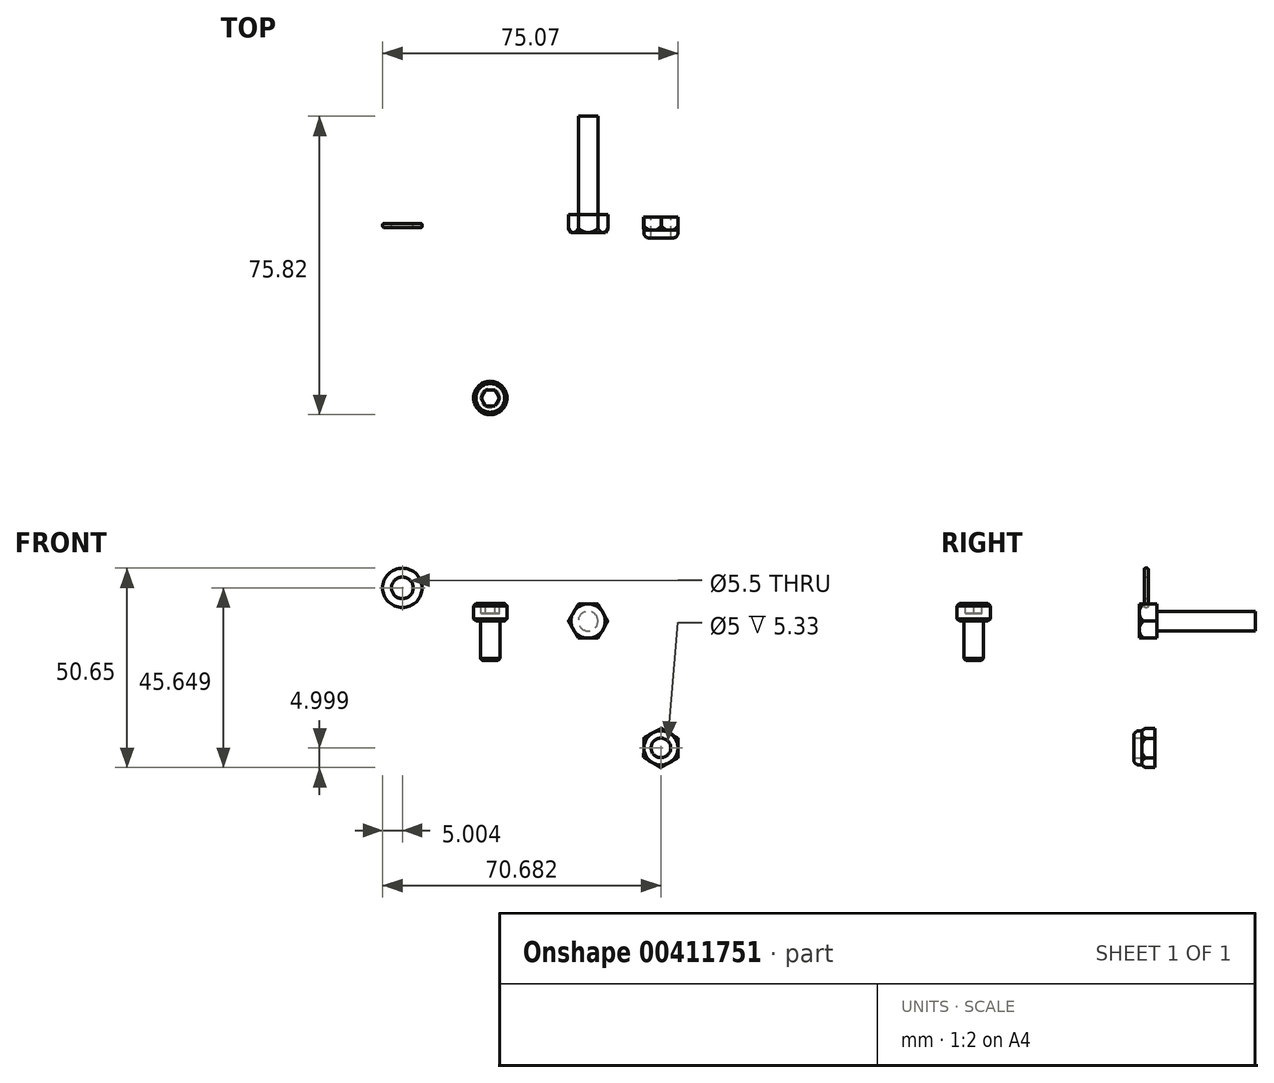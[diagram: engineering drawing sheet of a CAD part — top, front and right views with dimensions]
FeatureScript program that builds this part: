
annotation { "Feature Type Name" : "Feature", "Feature Type Description" : "" }
export const myFeature = defineFeature(function(context is Context, id is Id, definition is map)
    precondition{}
    {
        {
            var Q0;
            Q0=qCreatedBy(makeId("Front.planeOp"),FACE);
            var sketch = newSketch(context, id + "F0", { "sketchPlane" : qUnion([Q0])});
            skCircle(sketch, "E0.cCircle", {"center": v(0, 0) * mm, "radius": 4.33 * mm, "construction": true});
            skLineSegment(sketch, "E0.0", {"start": v(-2.5, 4.33) * mm, "end": v(2.5, 4.33) * mm});
            skLineSegment(sketch, "E0.1", {"start": v(2.5, 4.33) * mm, "end": v(5, 0) * mm});
            skLineSegment(sketch, "E0.2", {"start": v(5, 0) * mm, "end": v(2.5, -4.33) * mm});
            skLineSegment(sketch, "E0.3", {"start": v(2.5, -4.33) * mm, "end": v(-2.5, -4.33) * mm});
            skLineSegment(sketch, "E0.4", {"start": v(-2.5, -4.33) * mm, "end": v(-5, 0) * mm});
            skLineSegment(sketch, "E0.5", {"start": v(-5, 0) * mm, "end": v(-2.5, 4.33) * mm});
            skPoint(sketch, "E0.0.midPoint", {"position": v(0, 4.33) * mm});
            skSolve(sketch);
        }
        {
            var Q0;
            Q0=makeQuery(id+"F0.imprint","IMPRINT",FACE,{"disambiguationData":[TD([[makeQuery(id+"F0.imprint","IMPRINT",EDGE,{"derivedFrom":sQuery(id+"F0.wireOp",EDGE,"E0.0")}),-1.0]])]});
            extrude(context, id + "F1", {"entities" : qUnion([Q0]), "endBound" : BoundingType.SYMMETRIC, "depth" : 4.5 * mm});
        }
        {
            var Q0;
            Q0=makeQuery(id+"F1.opExtrude","SWEPT_FACE",FACE,{"disambiguationData":[OSD([sQuery(id+"F0.wireOp",EDGE,"E0.4")])]});
            var sketch = newSketch(context, id + "F2", { "sketchPlane" : qUnion([Q0])});
            skLineSegment(sketch, "E1", {"start": v(2.25, -2.5) * mm, "end": v(1.4, -2.5) * mm});
            skLineSegment(sketch, "E2", {"start": v(1.4, -2.5) * mm, "end": v(2.25, -1.9) * mm});
            skLineSegment(sketch, "E3", {"start": v(2.25, -1.9) * mm, "end": v(2.25, -2.5) * mm});
            skSolve(sketch);
        }
        {
            var Q0;
            Q0=qCreatedBy(makeId("Top.planeOp"),FACE);
            var sketch = newSketch(context, id + "F3", { "sketchPlane" : qUnion([Q0])});
            skLineSegment(sketch, "E4", {"start": v(5, -1.23) * mm, "end": v(5, -2.4) * mm});
            skLineSegment(sketch, "E5", {"start": v(5, -2.4) * mm, "end": v(4.27, -2.4) * mm});
            skLineSegment(sketch, "E6", {"start": v(4.27, -2.4) * mm, "end": v(5, -1.23) * mm});
            skSolve(sketch);
        }
        {
            var Q0;
            Q0=makeQuery(id+"F3.imprint","IMPRINT",FACE,{"disambiguationData":[TD([[makeQuery(id+"F3.imprint","IMPRINT",EDGE,{"derivedFrom":sQuery(id+"F3.wireOp",EDGE,"E4")}),-1.0]])]});
            var Q1;
            Q1=sQuery(id+"F0.wireOp",EDGE,"E0.cCircle");
            revolve(context, id + "F4", {"operationType" : NewBodyOperationType.REMOVE, "entities" : qUnion([Q0]), "axis" : qUnion([Q1]), "revolveType" : RevolveType.FULL, "oppositeDirection" : true});
        }
        {
            var Q0;
            Q0=makeQuery(id+"F1.opExtrude","CAP_FACE",FACE,{"disambiguationData":[OSD([sQuery(id+"F0.wireOp",EDGE,"E0.0"),sQuery(id+"F0.wireOp",EDGE,"E0.1"),sQuery(id+"F0.wireOp",EDGE,"E0.2"),sQuery(id+"F0.wireOp",EDGE,"E0.3"),sQuery(id+"F0.wireOp",EDGE,"E0.4"),sQuery(id+"F0.wireOp",EDGE,"E0.5")])],"isStart":true});
            var sketch = newSketch(context, id + "F5", { "sketchPlane" : qUnion([Q0])});
            skCircle(sketch, "E7", {"center": v(0, 0) * mm, "radius": 2.5 * mm});
            skSolve(sketch);
        }
        {
            var Q0;
            Q0=makeQuery(id+"F5.imprint","IMPRINT",FACE,{"disambiguationData":[TD([[makeQuery(id+"F5.imprint","IMPRINT",EDGE,{"derivedFrom":sQuery(id+"F5.wireOp",EDGE,"E7")}),1.0]])]});
            extrude(context, id + "F6", {"entities" : qUnion([Q0]), "operationType" : NewBodyOperationType.ADD, "depth" : 25 * mm});
        }
        {
            var Q0;
            Q0=qCreatedBy(makeId("Front.planeOp"),FACE);
            var sketch = newSketch(context, id + "F7", { "sketchPlane" : qUnion([Q0])});
            skCircle(sketch, "E8", {"center": v(-47.19, 8.45) * mm, "radius": 5 * mm});
            skCircle(sketch, "E9", {"center": v(-47.19, 8.45) * mm, "radius": 2.75 * mm});
            skSolve(sketch);
        }
        {
            var Q0;
            Q0=makeQuery(id+"F7.imprint","IMPRINT",FACE,{"disambiguationData":[TD([[makeQuery(id+"F7.imprint","IMPRINT",EDGE,{"derivedFrom":sQuery(id+"F7.wireOp",EDGE,"E8")}),1.0]])]});
            extrude(context, id + "F8", {"entities" : qUnion([Q0]), "depth" : 1 * mm});
        }
        {
            var Q0;
            Q0=makeQuery(id+"F8.opExtrude","CAP_EDGE",EDGE,{"disambiguationData":[OSD([sQuery(id+"F7.wireOp",EDGE,"E8")])],"isStart":false});
            var Q1;
            Q1=makeQuery(id+"F8.opExtrude","CAP_EDGE",EDGE,{"disambiguationData":[OSD([sQuery(id+"F7.wireOp",EDGE,"E8")])],"isStart":true});
            fillet(context, id + "F9", {"entities" : qUnion([Q0, Q1]), "radius" : 0.3 * mm, "tangentPropagation" : true, "allowEdgeOverflow" : false});
        }
        {
            var Q0;
            Q0=qCreatedBy(makeId("Front.planeOp"),FACE);
            var sketch = newSketch(context, id + "F10", { "sketchPlane" : qUnion([Q0])});
            skCircle(sketch, "E10.cCircle", {"center": v(18.5, -32.2) * mm, "radius": 4.33 * mm, "construction": true});
            skLineSegment(sketch, "E10.0", {"start": v(18.6, -27.2) * mm, "end": v(22.88, -29.8) * mm});
            skLineSegment(sketch, "E10.1", {"start": v(22.88, -29.8) * mm, "end": v(22.77, -34.8) * mm});
            skLineSegment(sketch, "E10.2", {"start": v(22.77, -34.8) * mm, "end": v(18.38, -37.2) * mm});
            skLineSegment(sketch, "E10.3", {"start": v(18.38, -37.2) * mm, "end": v(14.1, -34.6) * mm});
            skLineSegment(sketch, "E10.4", {"start": v(14.1, -34.6) * mm, "end": v(14.22, -29.6) * mm});
            skLineSegment(sketch, "E10.5", {"start": v(14.22, -29.6) * mm, "end": v(18.6, -27.2) * mm});
            skPoint(sketch, "E10.0.midPoint", {"position": v(20.74, -28.5) * mm});
            skCircle(sketch, "E11", {"center": v(18.5, -32.2) * mm, "radius": 2.5 * mm});
            skSolve(sketch);
        }
        {
            var Q0;
            Q0=makeQuery(id+"F10.imprint","IMPRINT",FACE,{"disambiguationData":[TD([[makeQuery(id+"F10.imprint","IMPRINT",EDGE,{"derivedFrom":sQuery(id+"F10.wireOp",EDGE,"E10.0")}),-1.0]])]});
            extrude(context, id + "F11", {"entities" : qUnion([Q0]), "endBound" : BoundingType.SYMMETRIC, "depth" : 3.33 * mm});
        }
        {
            var Q0;
            Q0=qCreatedBy(makeId("Right.planeOp"),FACE);
            cPlane(context, id + "F12", {"entities" : qUnion([Q0]), "cplaneType" : CPlaneType.OFFSET, "offset" : 18.4 * mm, "width" : 150 * mm, "height" : 150 * mm});
        }
        {
            var Q0;
            Q0=qCreatedBy(id+"F12.planeOp",FACE);
            var sketch = newSketch(context, id + "F13", { "sketchPlane" : qUnion([Q0])});
            skLineSegment(sketch, "E12", {"start": v(-0.6, -37.21) * mm, "end": v(-1.74, -37.21) * mm});
            skLineSegment(sketch, "E13", {"start": v(-1.74, -37.21) * mm, "end": v(-1.75, -36.57) * mm});
            skLineSegment(sketch, "E14", {"start": v(-1.75, -36.57) * mm, "end": v(-0.6, -37.21) * mm});
            skSolve(sketch);
        }
        {
            var Q0;
            Q0=makeQuery(id+"F13.imprint","IMPRINT",FACE,{"disambiguationData":[TD([[makeQuery(id+"F13.imprint","IMPRINT",EDGE,{"derivedFrom":sQuery(id+"F13.wireOp",EDGE,"E12")}),-1.0]])]});
            var Q1;
            Q1=makeQuery(id+"F11.opExtrude","CAP_EDGE",EDGE,{"disambiguationData":[OSD([sQuery(id+"F10.wireOp",EDGE,"E11")])],"isStart":false});
            revolve(context, id + "F14", {"operationType" : NewBodyOperationType.REMOVE, "entities" : qUnion([Q0]), "axis" : qUnion([Q1]), "revolveType" : RevolveType.FULL, "oppositeDirection" : true});
        }
        {
            var Q0;
            {var subQ0=sQuery(id+"F10.wireOp",EDGE,"E10.2");var subQ1=sQuery(id+"F10.wireOp",EDGE,"E10.1");var subQ2=sQuery(id+"F10.wireOp",EDGE,"E10.3");var subQ3=sQuery(id+"F10.wireOp",EDGE,"E10.0");var subQ4=sQuery(id+"F10.wireOp",EDGE,"E10.4");var subQ5=sQuery(id+"F10.wireOp",EDGE,"E10.5");var subQ6=sQuery(id+"F10.wireOp",EDGE,"E11");Q0=makeQuery(id+"F14.boolean.opBoolean","SPLIT",FACE,{"disambiguationData":[TD([makeQuery(id+"F11.opExtrude","SWEPT_FACE",FACE,{"disambiguationData":[OSD([subQ3])]}),makeQuery(id+"F11.opExtrude","SWEPT_FACE",FACE,{"disambiguationData":[OSD([subQ1])]}),makeQuery(id+"F11.opExtrude","SWEPT_FACE",FACE,{"disambiguationData":[OSD([subQ0])]}),makeQuery(id+"F11.opExtrude","SWEPT_FACE",FACE,{"disambiguationData":[OSD([subQ2])]}),makeQuery(id+"F11.opExtrude","SWEPT_FACE",FACE,{"disambiguationData":[OSD([subQ4])]}),makeQuery(id+"F11.opExtrude","SWEPT_FACE",FACE,{"disambiguationData":[OSD([subQ5])]}),makeQuery(id+"F11.opExtrude","SWEPT_FACE",FACE,{"disambiguationData":[OSD([subQ6])]}),makeQuery(id+"F14.opRevolve","SWEPT_FACE",FACE,{"disambiguationData":[OSD([sQuery(id+"F13.wireOp",EDGE,"E14")])]})])],"derivedFrom":makeQuery(id+"F11.opExtrude","CAP_FACE",FACE,{"disambiguationData":[OSD([subQ3,subQ1,subQ0,subQ2,subQ4,subQ5,subQ6])],"isStart":false})});}
            var sketch = newSketch(context, id + "F15", { "sketchPlane" : qUnion([Q0])});
            skCircle(sketch, "E15.0", {"center": v(18.5, -32.2) * mm, "radius": 4.33 * mm});
            skSolve(sketch);
        }
        {
            var Q0;
            {var subQ1=sQuery(id+"F10.wireOp",EDGE,"E11");Q0=makeQuery(id+"F15.imprint","IMPRINT",FACE,{"disambiguationData":[TD([[makeQuery(id+"F15.imprint","IMPRINT",EDGE,{"derivedFrom":makeQuery(id+"F11.opExtrude","CAP_EDGE",EDGE,{"disambiguationData":[OSD([subQ1])],"isStart":false})}),-1.0]])]});}
            extrude(context, id + "F16", {"entities" : qUnion([Q0]), "operationType" : NewBodyOperationType.ADD, "depth" : 2 * mm});
        }
        {
            var Q0;
            Q0=makeQuery(id+"F16.opExtrude","CAP_EDGE",EDGE,{"disambiguationData":[OSD([sQuery(id+"F15.wireOp",EDGE,"E15.0")])],"isStart":false});
            fillet(context, id + "F17", {"entities" : qUnion([Q0]), "radius" : 1.3 * mm, "tangentPropagation" : true, "allowEdgeOverflow" : false});
        }
        {
            var Q0;
            Q0=qCreatedBy(makeId("Top.planeOp"),FACE);
            var sketch = newSketch(context, id + "F18", { "sketchPlane" : qUnion([Q0])});
            skCircle(sketch, "E16", {"center": v(-24.87, -44.32) * mm, "radius": 4.25 * mm});
            skSolve(sketch);
        }
        {
            var Q0;
            Q0=makeQuery(id+"F18.imprint","IMPRINT",FACE,{"disambiguationData":[TD([[makeQuery(id+"F18.imprint","IMPRINT",EDGE,{"derivedFrom":sQuery(id+"F18.wireOp",EDGE,"E16")}),1.0]])]});
            extrude(context, id + "F19", {"entities" : qUnion([Q0]), "depth" : 4.5 * mm});
        }
        {
            var Q0;
            Q0=makeQuery(id+"F19.opExtrude","CAP_FACE",FACE,{"disambiguationData":[OSD([sQuery(id+"F18.wireOp",EDGE,"E16")])],"isStart":false});
            var sketch = newSketch(context, id + "F20", { "sketchPlane" : qUnion([Q0])});
            skCircle(sketch, "E17.cCircle", {"center": v(-24.87, -44.32) * mm, "radius": 2.07 * mm, "construction": true});
            skLineSegment(sketch, "E17.0", {"start": v(-23.66, -42.25) * mm, "end": v(-22.48, -44.33) * mm});
            skLineSegment(sketch, "E17.1", {"start": v(-22.48, -44.33) * mm, "end": v(-23.68, -46.4) * mm});
            skLineSegment(sketch, "E17.2", {"start": v(-23.68, -46.4) * mm, "end": v(-26.07, -46.38) * mm});
            skLineSegment(sketch, "E17.3", {"start": v(-26.07, -46.38) * mm, "end": v(-27.26, -44.3) * mm});
            skLineSegment(sketch, "E17.4", {"start": v(-27.26, -44.3) * mm, "end": v(-26.06, -42.24) * mm});
            skLineSegment(sketch, "E17.5", {"start": v(-26.06, -42.24) * mm, "end": v(-23.66, -42.25) * mm});
            skPoint(sketch, "E17.0.midPoint", {"position": v(-23.07, -43.29) * mm});
            skSolve(sketch);
        }
        {
            var Q0;
            Q0=makeQuery(id+"F19.opExtrude","CAP_EDGE",EDGE,{"disambiguationData":[OSD([sQuery(id+"F18.wireOp",EDGE,"E16")])],"isStart":false});
            var Q1;
            Q1=makeQuery(id+"F19.opExtrude","CAP_EDGE",EDGE,{"disambiguationData":[OSD([sQuery(id+"F18.wireOp",EDGE,"E16")])],"isStart":true});
            chamfer(context, id + "F21", {"entities" : qUnion([Q0, Q1]), "width" : 0.6 * mm, "tangentPropagation" : true});
        }
        {
            var Q0;
            Q0=makeQuery(id+"F20.imprint","IMPRINT",FACE,{"disambiguationData":[TD([[makeQuery(id+"F20.imprint","IMPRINT",EDGE,{"derivedFrom":sQuery(id+"F20.wireOp",EDGE,"E17.0")}),-1.0]])]});
            extrude(context, id + "F22", {"entities" : qUnion([Q0]), "operationType" : NewBodyOperationType.REMOVE, "oppositeDirection" : true, "depth" : 2.6 * mm});
        }
        {
            var Q0;
            Q0=makeQuery(id+"F19.opExtrude","CAP_FACE",FACE,{"disambiguationData":[OSD([sQuery(id+"F18.wireOp",EDGE,"E16")])],"isStart":true});
            var sketch = newSketch(context, id + "F23", { "sketchPlane" : qUnion([Q0])});
            skCircle(sketch, "E18", {"center": v(-24.87, 44.32) * mm, "radius": 2.5 * mm});
            skSolve(sketch);
        }
        {
            var Q0;
            Q0=makeQuery(id+"F23.imprint","IMPRINT",FACE,{"disambiguationData":[TD([[makeQuery(id+"F23.imprint","IMPRINT",EDGE,{"derivedFrom":sQuery(id+"F23.wireOp",EDGE,"E18")}),1.0]])]});
            extrude(context, id + "F24", {"entities" : qUnion([Q0]), "operationType" : NewBodyOperationType.ADD, "depth" : 10 * mm});
        }
        {
            var Q0;
            Q0=makeQuery(id+"F24.opExtrude","CAP_EDGE",EDGE,{"disambiguationData":[OSD([sQuery(id+"F23.wireOp",EDGE,"E18")])],"isStart":false});
            chamfer(context, id + "F25", {"entities" : qUnion([Q0]), "width" : 0.5 * mm, "tangentPropagation" : true});
        }
    });
